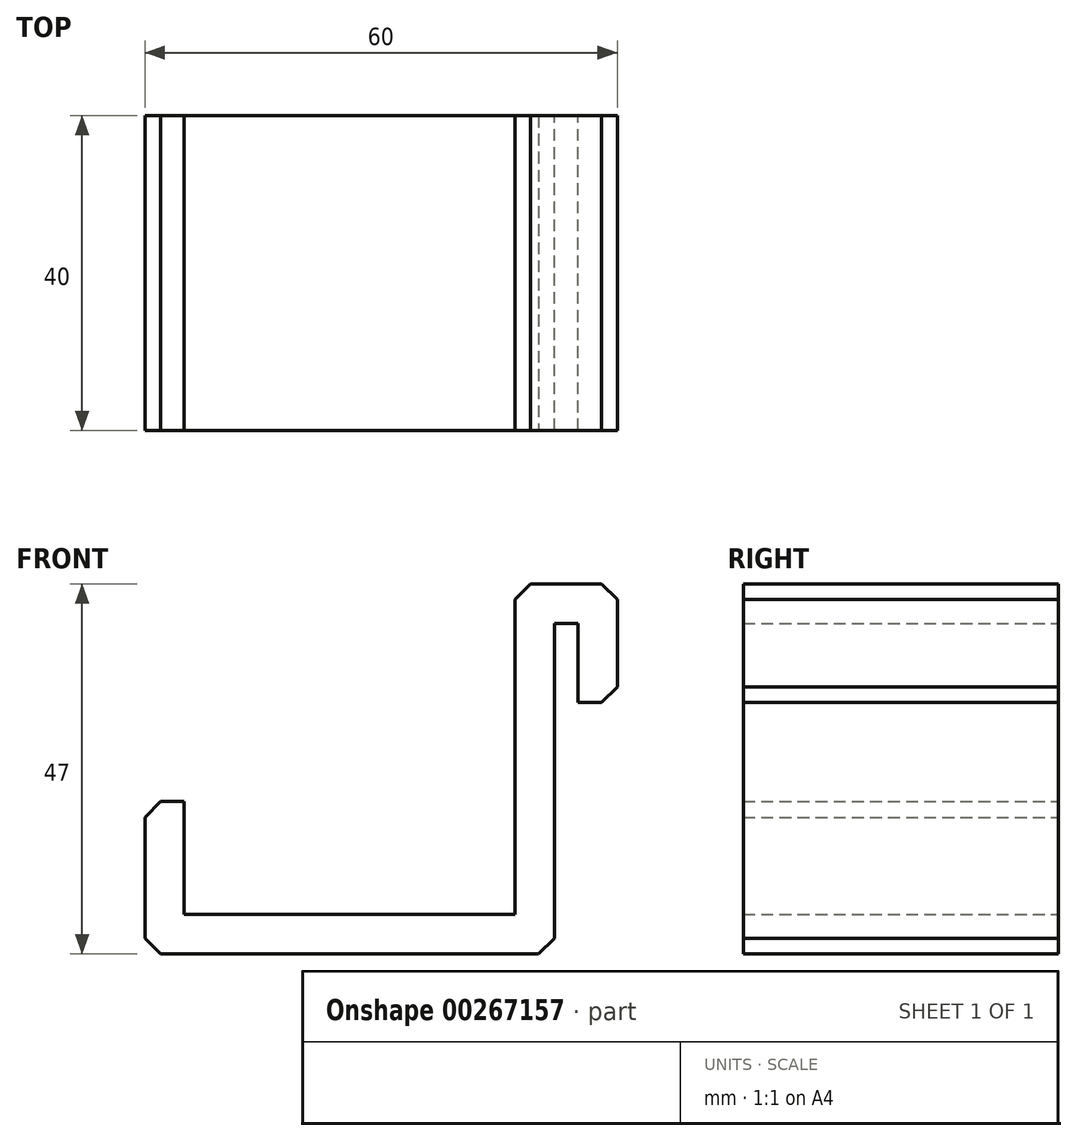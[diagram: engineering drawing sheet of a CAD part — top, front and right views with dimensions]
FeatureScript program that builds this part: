
annotation { "Feature Type Name" : "Feature", "Feature Type Description" : "" }
export const myFeature = defineFeature(function(context is Context, id is Id, definition is map)
    precondition{}
    {
        {
            var Q0;
            Q0=qCreatedBy(makeId("Front.planeOp"),FACE);
            var sketch = newSketch(context, id + "F0", { "sketchPlane" : qUnion([Q0])});
            skLineSegment(sketch, "E0", {"start": v(7.9, 24.92) * mm, "end": v(12.9, 24.92) * mm});
            skLineSegment(sketch, "E1", {"start": v(12.9, 24.92) * mm, "end": v(12.9, 40) * mm});
            skLineSegment(sketch, "E2", {"start": v(12.9, 40) * mm, "end": v(-0.1, 40) * mm});
            skLineSegment(sketch, "E3", {"start": v(-0.1, 40) * mm, "end": v(-0.1, -2) * mm});
            skLineSegment(sketch, "E4", {"start": v(-0.1, -2) * mm, "end": v(-42.1, -2) * mm});
            skLineSegment(sketch, "E5", {"start": v(-42.1, -2) * mm, "end": v(-42.1, 12.35) * mm});
            skLineSegment(sketch, "E6", {"start": v(-42.1, 12.35) * mm, "end": v(-47.1, 12.35) * mm});
            skLineSegment(sketch, "E7", {"start": v(-47.1, 12.35) * mm, "end": v(-47.1, -7) * mm});
            skLineSegment(sketch, "E8", {"start": v(-47.1, -7) * mm, "end": v(4.9, -7) * mm});
            skLineSegment(sketch, "E9", {"start": v(4.9, -7) * mm, "end": v(4.9, 35) * mm});
            skLineSegment(sketch, "E10", {"start": v(4.9, 35) * mm, "end": v(7.9, 35) * mm});
            skLineSegment(sketch, "E11", {"start": v(7.9, 35) * mm, "end": v(7.9, 24.92) * mm});
            skSolve(sketch);
        }
        {
            var Q0;
            Q0=makeQuery(id+"F0.imprint","IMPRINT",FACE,{"disambiguationData":[TD([[makeQuery(id+"F0.imprint","IMPRINT",EDGE,{"derivedFrom":sQuery(id+"F0.wireOp",EDGE,"E0")}),1.0]])]});
            extrude(context, id + "F1", {"entities" : qUnion([Q0]), "depth" : 40 * mm});
        }
        {
            var Q0;
            Q0=makeQuery(id+"F1.opExtrude","SWEPT_EDGE",EDGE,{"disambiguationData":[OSD([sQuery(id+"F0.wireOp",EDGE,"E2"),sQuery(id+"F0.wireOp",EDGE,"E3")])]});
            var Q1;
            Q1=makeQuery(id+"F1.opExtrude","SWEPT_EDGE",EDGE,{"disambiguationData":[OSD([sQuery(id+"F0.wireOp",EDGE,"E1"),sQuery(id+"F0.wireOp",EDGE,"E2")])]});
            var Q2;
            Q2=makeQuery(id+"F1.opExtrude","SWEPT_EDGE",EDGE,{"disambiguationData":[OSD([sQuery(id+"F0.wireOp",EDGE,"E6"),sQuery(id+"F0.wireOp",EDGE,"E7")])]});
            var Q3;
            Q3=makeQuery(id+"F1.opExtrude","SWEPT_EDGE",EDGE,{"disambiguationData":[OSD([sQuery(id+"F0.wireOp",EDGE,"E7"),sQuery(id+"F0.wireOp",EDGE,"E8")])]});
            var Q4;
            Q4=makeQuery(id+"F1.opExtrude","SWEPT_EDGE",EDGE,{"disambiguationData":[OSD([sQuery(id+"F0.wireOp",EDGE,"E8"),sQuery(id+"F0.wireOp",EDGE,"E9")])]});
            var Q5;
            Q5=makeQuery(id+"F1.opExtrude","SWEPT_EDGE",EDGE,{"disambiguationData":[OSD([sQuery(id+"F0.wireOp",EDGE,"E0"),sQuery(id+"F0.wireOp",EDGE,"E1")])]});
            chamfer(context, id + "F2", {"entities" : qUnion([Q0, Q1, Q2, Q3, Q4, Q5]), "width" : 2 * mm, "tangentPropagation" : true});
        }
    });
